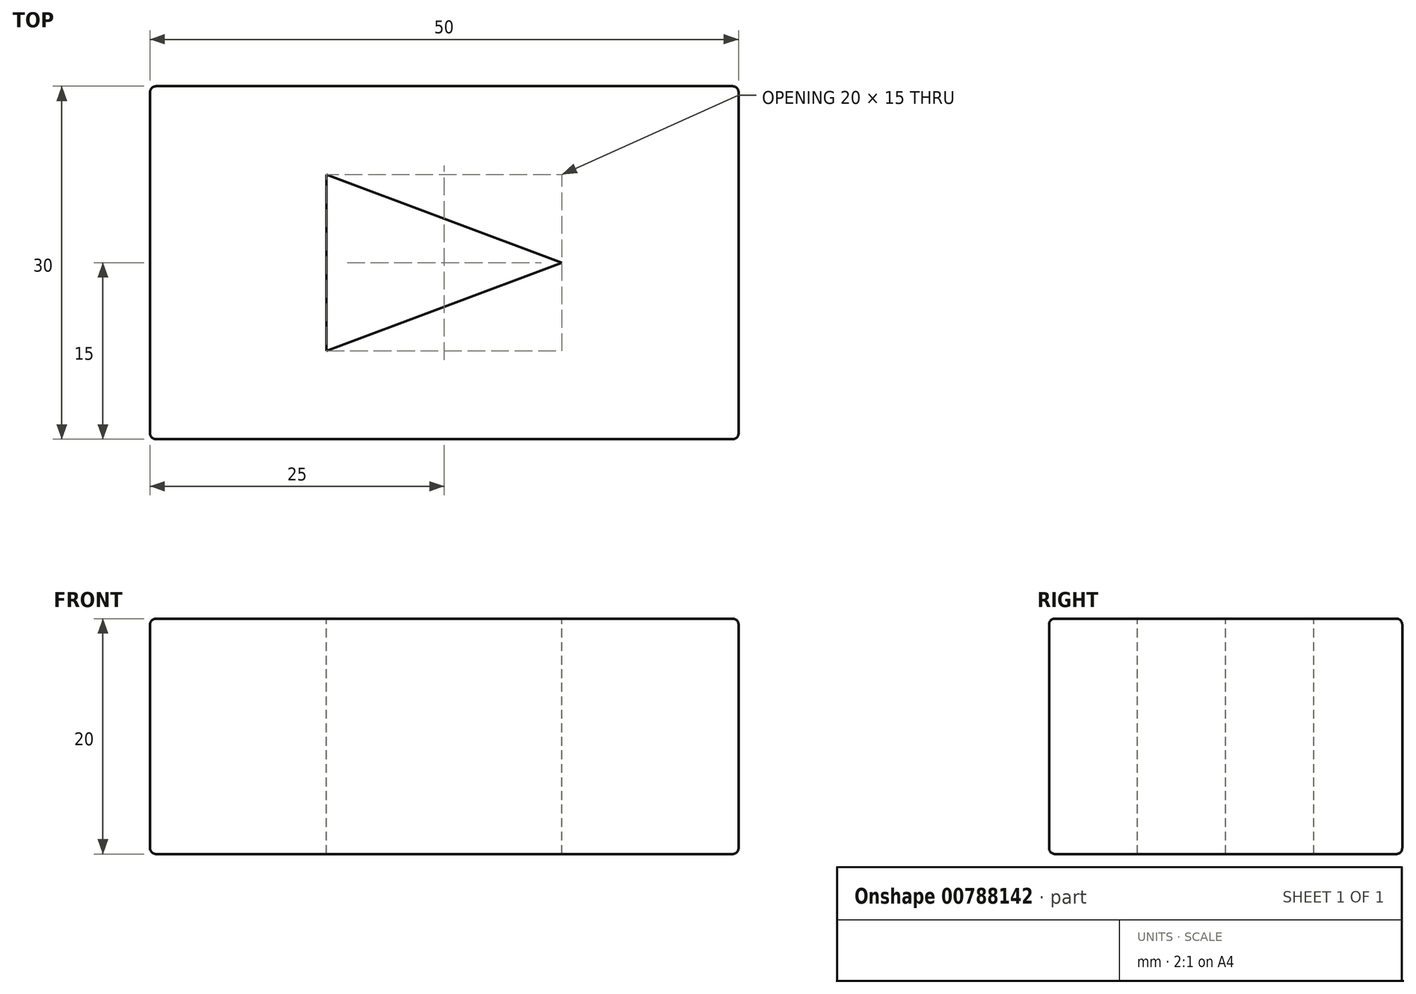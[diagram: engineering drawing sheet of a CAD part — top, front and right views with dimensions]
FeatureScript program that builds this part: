
annotation { "Feature Type Name" : "Feature", "Feature Type Description" : "" }
export const myFeature = defineFeature(function(context is Context, id is Id, definition is map)
    precondition{}
    {
        {
            var Q0;
            Q0=qCreatedBy(makeId("Top.planeOp"),FACE);
            var sketch = newSketch(context, id + "F0", { "sketchPlane" : qUnion([Q0])});
            skLineSegment(sketch, "E0.bottom", {"start": v(25, 15) * mm, "end": v(-25, 15) * mm});
            skLineSegment(sketch, "E0.top", {"start": v(25, -15) * mm, "end": v(-25, -15) * mm});
            skLineSegment(sketch, "E0.left", {"start": v(25, 15) * mm, "end": v(25, -15) * mm});
            skLineSegment(sketch, "E0.right", {"start": v(-25, 15) * mm, "end": v(-25, -15) * mm});
            skPoint(sketch, "E0.middle", {"position": v(0, 0) * mm});
            skSolve(sketch);
        }
        {
            var Q0;
            Q0=makeQuery(id+"F0.imprint","IMPRINT",FACE,{"disambiguationData":[TD([[makeQuery(id+"F0.imprint","IMPRINT",EDGE,{"derivedFrom":sQuery(id+"F0.wireOp",EDGE,"E0.bottom")}),1.0]])]});
            extrude(context, id + "F1", {"entities" : qUnion([Q0]), "depth" : 20 * mm, "offsetDistance" : 25 * mm});
        }
        {
            var Q0;
            Q0=makeQuery(id+"F1.opExtrude","CAP_FACE",FACE,{"disambiguationData":[OSD([sQuery(id+"F0.wireOp",EDGE,"E0.bottom"),sQuery(id+"F0.wireOp",EDGE,"E0.top"),sQuery(id+"F0.wireOp",EDGE,"E0.left"),sQuery(id+"F0.wireOp",EDGE,"E0.right")])],"isStart":false});
            var sketch = newSketch(context, id + "F2", { "sketchPlane" : qUnion([Q0])});
            skLineSegment(sketch, "E1", {"start": v(-10, 7.5) * mm, "end": v(10, 0) * mm});
            skLineSegment(sketch, "E2", {"start": v(-10, -7.5) * mm, "end": v(10, 0) * mm});
            skLineSegment(sketch, "E3", {"start": v(-10, 7.5) * mm, "end": v(-10, -7.5) * mm});
            skSolve(sketch);
        }
        {
            var Q0;
            Q0=makeQuery(id+"F2.imprint","IMPRINT",FACE,{"disambiguationData":[TD([[makeQuery(id+"F2.imprint","IMPRINT",EDGE,{"derivedFrom":sQuery(id+"F2.wireOp",EDGE,"E1")}),-1.0]])]});
            extrude(context, id + "F3", {"entities" : qUnion([Q0]), "operationType" : NewBodyOperationType.REMOVE, "endBound" : BoundingType.THROUGH_ALL, "oppositeDirection" : true, "depth" : 25 * mm, "offsetDistance" : 25 * mm});
        }
        {
            var Q0;
            Q0=makeQuery(id+"F1.opExtrude","SWEPT_FACE",FACE,{"disambiguationData":[OSD([sQuery(id+"F0.wireOp",EDGE,"E0.top")])]});
            var Q1;
            Q1=makeQuery(id+"F1.opExtrude","SWEPT_FACE",FACE,{"disambiguationData":[OSD([sQuery(id+"F0.wireOp",EDGE,"E0.right")])]});
            var Q2;
            Q2=makeQuery(id+"F1.opExtrude","SWEPT_FACE",FACE,{"disambiguationData":[OSD([sQuery(id+"F0.wireOp",EDGE,"E0.left")])]});
            var Q3;
            Q3=makeQuery(id+"F1.opExtrude","SWEPT_FACE",FACE,{"disambiguationData":[OSD([sQuery(id+"F0.wireOp",EDGE,"E0.bottom")])]});
            fillet(context, id + "F4", {"entities" : qUnion([Q0, Q1, Q2, Q3]), "radius" : 0.5 * mm, "tangentPropagation" : true, "allowEdgeOverflow" : false});
        }
    });
